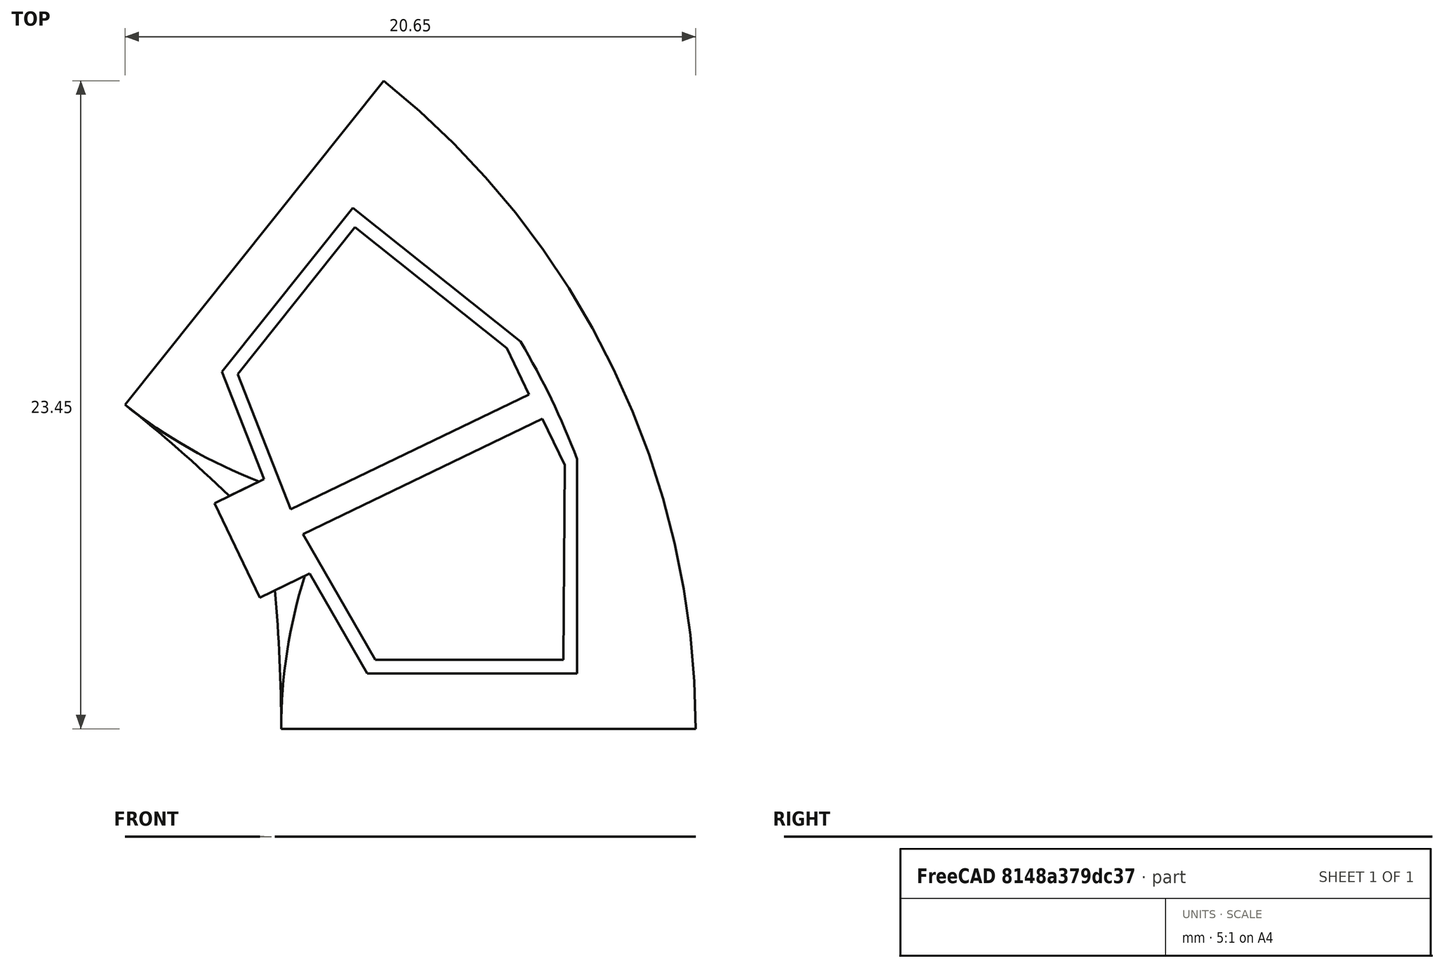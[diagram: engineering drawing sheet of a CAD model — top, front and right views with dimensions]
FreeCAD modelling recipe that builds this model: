
FCSTD DOCUMENT  (FreeCAD 0.18R4 (GitTag))
Label: StatorIRNeedleWinding
License: All rights reserved
LicenseURL: http://en.wikipedia.org/wiki/All_rights_reserved
objects: Sketcher::SketchObject×8, Surface::Filling×5, PartDesign::Body×2, Spreadsheet::Sheet×1
note: 15 computed .brp shape members not serialized (recipe doc carries the construction recipe); baked Part::Feature solids carry a one-line shape summary decoded from their .brp

FEATURE [Spreadsheet::Sheet] Spreadsheet  label="Variables"
  cells = A2=slotNumber; B2(slotNumber)=7; A3=outerDiameter; B3(outerDiameter)=60; A4=innerDiameter; B4(innerDiameter)=30; A5=stackLength; B5(stackLength)=20; A6=stackingFactor; B6(stackingFactor)=0.95; A7=cuttingThickness; B7(cuttingThickness)=0.1; A8=skewAngle; B8(skewAngle)=0; A9=segmentAngle; B9(segmentAngle)==360 / slotNumber; A10=tipHeightReduction; B10(tipHeightReduction)=90; A11=toothThickness; B11(toothThickness)=4; A12=yokeThickness; B12(yokeThickness)=2.5; A13=tipHeight; B13(tipHeight)=2; A14=tipAngle; B14(tipAngle)=120; A15=openingLeft; B15(openingLeft)=1.9; A16=openingRight; B16(openingRight)=1.9; A17=slotIsolation; B17(slotIsolation)=0.5; A18=windingAngle; B18(windingAngle)=35; A19=heightRatio; B19(heightRatio)=45; A20=roundingRadii; B20(roundingRadii)=0.2; A21=backWidth; B21(backWidth)=4.72; A22=backAngle; B22(backAngle)=90; A23=phaseSeparation; B23(phaseSeparation)=1
FEATURE [Sketcher::SketchObject] Sketch003  label="StatorSketch1"
  MapMode = 5
  Support = -> [XY_Plane]
  expr: Constraints[76] = Variables.backWidth
  expr: Constraints[37] = Variables.tipAngle
  expr: Constraints[60] = Variables.backAngle
  expr: Constraints[30] = Variables.tipHeight
  expr: Constraints[28] = Variables.openingRight
  expr: Constraints[32] = Variables.tipHeight * (1 - Variables.tipHeightReduction / 100)
  expr: Constraints[22] = Variables.openingLeft
  expr: Constraints[6] = Variables.outerDiameter / 2
  expr: Constraints[59] = Variables.tipHeight
  expr: Constraints[5] = Variables.segmentAngle
  expr: Constraints[11] = Variables.innerDiameter / 2
  expr: Constraints[54] = Variables.outerDiameter / 2 - Variables.yokeThickness
  expr: Constraints[49] = Variables.tipHeight * (1 - Variables.tipHeightReduction / 100)
  expr: Constraints[58] = Variables.toothThickness / 2
  expr: Constraints[18] = Variables.segmentAngle / 2
  expr: Constraints[50] = Variables.tipAngle
  expr: Constraints[52] = Variables.backAngle
  expr: Constraints[42] = Variables.toothThickness / 2
  sketch-geometry (27):
    g0: LineSegment [constr] StartX=0 StartY=0 StartZ=0 EndX=18.7047 EndY=23.4549 EndZ=0
    g1: LineSegment [constr] StartX=0 StartY=0 StartZ=0 EndX=30 EndY=0 EndZ=0
    g2: ArcOfCircle CenterX=0 CenterY=0 CenterZ=0 NormalX=0 NormalY=0 NormalZ=1 AngleXU=0 Radius=30 StartAngle=0 EndAngle=0.897598
    g3: ArcOfCircle [constr] CenterX=0 CenterY=0 CenterZ=0 NormalX=0 NormalY=0 NormalZ=1 AngleXU=0 Radius=15 StartAngle=0 EndAngle=0.897598
    g4: LineSegment [constr] StartX=12.5834 StartY=8.16445 StartZ=0 EndX=26.1523 EndY=14.6989 EndZ=0
    g5: LineSegment [constr] StartX=14.2288 StartY=4.74764 StartZ=0 EndX=27.7977 EndY=11.2821 EndZ=0
    g6: LineSegment [constr] StartX=27.0291 StartY=13.0165 StartZ=0 EndX=13.5145 EndY=6.50826 EndZ=0
    g7: LineSegment [constr] StartX=0 StartY=0 StartZ=0 EndX=13.5145 EndY=6.50826 EndZ=0
    g8: LineSegment [constr] StartX=12.5834 StartY=8.16445 StartZ=0 EndX=13.5145 EndY=6.50826 EndZ=0
    g9: LineSegment [constr] StartX=13.5145 StartY=6.50826 StartZ=0 EndX=14.2288 EndY=4.74764 EndZ=0
    g10: LineSegment [constr] StartX=13.124 StartY=8.42478 StartZ=0 EndX=14.3853 EndY=9.03222 EndZ=0
    g11: LineSegment StartX=13.124 StartY=8.42478 StartZ=0 EndX=14.3853 EndY=9.03222 EndZ=0
    g12: LineSegment StartX=14.3853 StartY=9.03222 StartZ=0 EndX=12.8601 EndY=12.9183 EndZ=0
    g13: LineSegment StartX=12.8601 StartY=12.9183 StartZ=0 EndX=17.5931 EndY=18.8533 EndZ=0
    g14: LineSegment [constr] StartX=12.8601 StartY=12.9183 StartZ=0 EndX=11.2965 EndY=14.1653 EndZ=0
    g15: LineSegment StartX=17.5931 StartY=18.8533 StartZ=0 EndX=23.6613 EndY=14.0141 EndZ=0
    g16: LineSegment StartX=25.7092 StartY=9.7615 StartZ=0 EndX=25.7092 EndY=2 EndZ=0
    g17: LineSegment StartX=25.7092 StartY=2 StartZ=0 EndX=18.1181 EndY=2 EndZ=0
    g18: LineSegment StartX=18.1181 StartY=2 StartZ=0 EndX=16.0308 EndY=5.61541 EndZ=0
    g19: LineSegment StartX=16.0308 StartY=5.61541 StartZ=0 EndX=14.7694 EndY=5.00797 EndZ=0
    g20: LineSegment [constr] StartX=25.7092 StartY=2 StartZ=0 EndX=25.7092 EndY=0 EndZ=0
    g21: LineSegment StartX=9.35235 StartY=11.7275 StartZ=0 EndX=18.7047 EndY=23.4549 EndZ=0
    g22: LineSegment StartX=30 StartY=0 StartZ=0 EndX=15 EndY=0 EndZ=0
    g23: ArcOfCircle CenterX=-39.4998 CenterY=0 CenterZ=0 NormalX=0 NormalY=0 NormalZ=1 AngleXU=0 Radius=54.4998 StartAngle=0 EndAngle=0.0920195
    g24: ArcOfCircle CenterX=-24.6277 CenterY=-30.8822 CenterZ=0 NormalX=0 NormalY=0 NormalZ=1 AngleXU=0 Radius=54.4998 StartAngle=0.805578 EndAngle=0.897598
    g25: ArcOfCircle CenterX=0 CenterY=0 CenterZ=0 NormalX=0 NormalY=0 NormalZ=1 AngleXU=0 Radius=27.5 StartAngle=0.362875 EndAngle=0.534723
    g26: LineSegment [constr] StartX=23.6613 StartY=14.0141 StartZ=0 EndX=25.7092 EndY=9.7615 EndZ=0
  constraints (77):
    c: Angle(g-1,g1) = 0
    c: Coincident(g0,g-1)
    c: Coincident(g1,g-1)
    c: Coincident(g2,g-1)
    c: Coincident(g2,g0)
    c: Angle(g1,g0) = 0.897598
    c: Radius(g2) = 30
    c: Coincident(g2,g1)
    c: Coincident(g3,g-1)
    c: PointOnObject(g3,g1)
    c: PointOnObject(g3,g0)
    c: Radius(g3) = 15
    c: PointOnObject(g4,g3)
    c: PointOnObject(g4,g2)
    c: PointOnObject(g5,g3)
    c: PointOnObject(g5,g2)
    c: PointOnObject(g6,g2)
    c: PointOnObject(g6,g3)
    c: Angle(g1,g6) = 0.448799
    c: Coincident(g7,g-1)
    c: Coincident(g7,g6)
    c: Coincident(g8,g4)
    c: Distance(g8) = 1.9
    c: Coincident(g8,g6)
    c: Parallel(g4,g6)
    c: Parallel(g5,g6)
    c: Coincident(g9,g6)
    c: Coincident(g9,g5)
    c: Distance(g9) = 1.9
    c: PointOnObject(g10,g4)
    c: Distance(g4,g10) = 2
    c: Angle(g4,g10) = 3.14159
    c: Distance(g10,g10) = 0.2
    c: Coincident(g11,g10)
    c: Coincident(g12,g11)
    c: Coincident(g13,g12)
    c: Coincident(g11,g10)
    c: Angle(g12,g13) = 2.0944
    c: Parallel(g0,g13)
    c: Coincident(g14,g12)
    c: PointOnObject(g14,g0)
    c: Angle(g13,g14) = 1.5708
    c: Distance(g14) = 2
    c: Coincident(g15,g13)
    c: Coincident(g17,g16)
    c: Coincident(g18,g17)
    c: PointOnObject(g18,g5)
    c: Coincident(g19,g18)
    c: PointOnObject(g19,g5)
    c: Distance(g19) = 0.2
    c: Angle(g17,g18) = 2.0944
    c: Parallel(g17,g1)
    c: Angle(g16,g17) = 1.5708
    c: Symmetric(g15,g16,g6)
    c: Distance(g-1,g15) = 27.5
    c: Coincident(g20,g16)
    c: PointOnObject(g20,g1)
    c: Vertical(g20)
    c: DistanceY(g20,g20) = 2
    c: Distance(g5,g18) = 2
    c: Angle(g13,g15) = 1.5708
    c: Coincident(g21,g3)
    c: Coincident(g21,g0)
    c: Coincident(g22,g2)
    c: Coincident(g22,g3)
    c: PointOnObject(g23,g-1)
    c: Coincident(g23,g19)
    c: Coincident(g23,g22)
    c: PointOnObject(g24,g0)
    c: Coincident(g24,g11)
    c: Coincident(g24,g21)
    c: Coincident(g25,g2)
    c: Coincident(g25,g15)
    c: Coincident(g25,g16)
    c: Coincident(g26,g15)
    c: Coincident(g26,g16)
    c: Distance(g26) = 4.72
FEATURE [Sketcher::SketchObject] Sketch  label="StatorStack"
  MapMode = 5
  Support = -> [XY_Plane001]
  expr: Constraints[20] = Variables.innerDiameter / 2
  expr: Constraints[10] = Variables.outerDiameter / 2
  expr: Constraints[9] = Variables.innerDiameter / 2
  expr: Constraints[8] = Variables.stackLength
  sketch-geometry (8):
    g0: LineSegment StartX=-10 StartY=15 StartZ=0 EndX=10 EndY=15 EndZ=0
    g1: LineSegment StartX=10 StartY=15 StartZ=0 EndX=10 EndY=30 EndZ=0
    g2: LineSegment StartX=10 StartY=30 StartZ=0 EndX=-10 EndY=30 EndZ=0
    g3: LineSegment StartX=-10 StartY=30 StartZ=0 EndX=-10 EndY=15 EndZ=0
    g4: LineSegment StartX=-10 StartY=-15 StartZ=0 EndX=10 EndY=-15 EndZ=0
    g5: LineSegment StartX=10 StartY=-15 StartZ=0 EndX=10 EndY=-30 EndZ=0
    g6: LineSegment StartX=10 StartY=-30 StartZ=0 EndX=-10 EndY=-30 EndZ=0
    g7: LineSegment StartX=-10 StartY=-30 StartZ=0 EndX=-10 EndY=-15 EndZ=0
  constraints (22):
    c: Coincident(g0,g1)
    c: Coincident(g1,g2)
    c: Coincident(g2,g3)
    c: Coincident(g3,g0)
    c: Horizontal(g2)
    c: Vertical(g1)
    c: Vertical(g3)
    c: Symmetric(g0,g0,g-2)
    c: DistanceX(g0,g0) = 20
    c: DistanceY(g-1,g0) = 15
    c: DistanceY(g-1,g1) = 30
    c: Coincident(g4,g5)
    c: Coincident(g5,g6)
    c: Coincident(g6,g7)
    c: Coincident(g7,g4)
    c: Horizontal(g6)
    c: Vertical(g5)
    c: Vertical(g7)
    c: Equal(g4,g0)
    c: Symmetric(g4,g4,g-2)
    c: DistanceY(g4,g-1) = 15
    c: Equal(g7,g3)
FEATURE [PartDesign::Body] Body001  label="SideView"
  Group = -> [Sketch]
  Origin = -> Origin001
FEATURE [Sketcher::SketchObject] Sketch005  label="StatorSketch2"
  MapMode = 5
  Support = -> [XY_Plane]
  expr: Constraints[76] = Variables.backWidth
  expr: Constraints[30] = Variables.tipHeight
  expr: Constraints[51] = Variables.tipAngle
  expr: Constraints[28] = Variables.openingRight
  expr: Constraints[37] = Variables.tipAngle
  expr: Constraints[60] = Variables.tipHeight
  expr: Constraints[32] = Variables.tipHeight * (1 - Variables.tipHeightReduction / 100)
  expr: Constraints[61] = Variables.backAngle
  expr: Constraints[6] = Variables.outerDiameter / 2
  expr: Constraints[5] = Variables.segmentAngle
  expr: Constraints[22] = Variables.openingLeft
  expr: Constraints[55] = Variables.outerDiameter / 2 - Variables.yokeThickness
  expr: Constraints[59] = Variables.toothThickness / 2
  expr: Constraints[50] = Variables.tipHeight * (1 - Variables.tipHeightReduction / 100)
  expr: Constraints[18] = Variables.segmentAngle / 2
  expr: Constraints[11] = Variables.innerDiameter / 2
  expr: Constraints[53] = Variables.backAngle
  expr: Constraints[42] = Variables.toothThickness / 2
  sketch-geometry (27):
    g0: LineSegment [constr] StartX=0 StartY=0 StartZ=0 EndX=18.7047 EndY=23.4549 EndZ=0
    g1: LineSegment [constr] StartX=0 StartY=0 StartZ=0 EndX=30 EndY=0 EndZ=0
    g2: ArcOfCircle CenterX=0 CenterY=0 CenterZ=0 NormalX=0 NormalY=0 NormalZ=1 AngleXU=0 Radius=30 StartAngle=0 EndAngle=0.897598
    g3: ArcOfCircle [constr] CenterX=0 CenterY=0 CenterZ=0 NormalX=0 NormalY=0 NormalZ=1 AngleXU=0 Radius=15 StartAngle=0 EndAngle=0.897598
    g4: LineSegment [constr] StartX=12.5834 StartY=8.16445 StartZ=0 EndX=26.1523 EndY=14.6989 EndZ=0
    g5: LineSegment [constr] StartX=14.2288 StartY=4.74764 StartZ=0 EndX=27.7977 EndY=11.2821 EndZ=0
    g6: LineSegment [constr] StartX=27.0291 StartY=13.0165 StartZ=0 EndX=13.5145 EndY=6.50826 EndZ=0
    g7: LineSegment [constr] StartX=0 StartY=0 StartZ=0 EndX=13.5145 EndY=6.50826 EndZ=0
    g8: LineSegment [constr] StartX=12.5834 StartY=8.16445 StartZ=0 EndX=13.5145 EndY=6.50826 EndZ=0
    g9: LineSegment [constr] StartX=13.5145 StartY=6.50826 StartZ=0 EndX=14.2288 EndY=4.74764 EndZ=0
    g10: LineSegment [constr] StartX=14.2051 StartY=8.94544 StartZ=0 EndX=14.3853 EndY=9.03222 EndZ=0
    g11: LineSegment StartX=14.2051 StartY=8.94544 StartZ=0 EndX=14.3853 EndY=9.03222 EndZ=0
    g12: LineSegment StartX=14.3853 StartY=9.03222 StartZ=0 EndX=12.8601 EndY=12.9183 EndZ=0
    g13: LineSegment StartX=12.8601 StartY=12.9183 StartZ=0 EndX=17.5931 EndY=18.8533 EndZ=0
    g14: LineSegment [constr] StartX=12.8601 StartY=12.9183 StartZ=0 EndX=11.2965 EndY=14.1653 EndZ=0
    g15: LineSegment StartX=17.5931 StartY=18.8533 StartZ=0 EndX=23.6613 EndY=14.0141 EndZ=0
    g16: LineSegment [constr] StartX=23.6613 StartY=14.0141 StartZ=0 EndX=25.7092 EndY=9.7615 EndZ=0
    g17: LineSegment StartX=25.7092 StartY=9.7615 StartZ=0 EndX=25.7092 EndY=2 EndZ=0
    g18: LineSegment StartX=25.7092 StartY=2 StartZ=0 EndX=18.1181 EndY=2 EndZ=0
    g19: LineSegment StartX=18.1181 StartY=2 StartZ=0 EndX=16.0308 EndY=5.61541 EndZ=0
    g20: LineSegment StartX=16.0308 StartY=5.61541 StartZ=0 EndX=15.8506 EndY=5.52863 EndZ=0
    g21: LineSegment [constr] StartX=25.7092 StartY=2 StartZ=0 EndX=25.7092 EndY=0 EndZ=0
    g22: LineSegment StartX=9.35235 StartY=11.7275 StartZ=0 EndX=18.7047 EndY=23.4549 EndZ=0
    g23: LineSegment StartX=30 StartY=0 StartZ=0 EndX=15 EndY=0 EndZ=0
    g24: ArcOfCircle CenterX=20.8201 CenterY=26.1075 CenterZ=0 NormalX=0 NormalY=0 NormalZ=1 AngleXU=0 Radius=18.3928 StartAngle=4.03919 EndAngle=4.3445
    g25: ArcOfCircle CenterX=33.3928 CenterY=0 CenterZ=0 NormalX=0 NormalY=0 NormalZ=1 AngleXU=0 Radius=18.3928 StartAngle=2.83628 EndAngle=3.14159
    g26: ArcOfCircle CenterX=0 CenterY=0 CenterZ=0 NormalX=0 NormalY=0 NormalZ=1 AngleXU=0 Radius=27.5 StartAngle=0.362875 EndAngle=0.534723
  constraints (77):
    c: Angle(g-1,g1) = 0
    c: Coincident(g0,g-1)
    c: Coincident(g1,g-1)
    c: Coincident(g2,g-1)
    c: Coincident(g2,g0)
    c: Angle(g1,g0) = 0.897598
    c: Radius(g2) = 30
    c: Coincident(g2,g1)
    c: Coincident(g3,g-1)
    c: PointOnObject(g3,g1)
    c: PointOnObject(g3,g0)
    c: Radius(g3) = 15
    c: PointOnObject(g4,g3)
    c: PointOnObject(g4,g2)
    c: PointOnObject(g5,g3)
    c: PointOnObject(g5,g2)
    c: PointOnObject(g6,g2)
    c: PointOnObject(g6,g3)
    c: Angle(g1,g6) = 0.448799
    c: Coincident(g7,g-1)
    c: Coincident(g7,g6)
    c: Coincident(g8,g4)
    c: Distance(g8) = 1.9
    c: Coincident(g8,g6)
    c: Parallel(g4,g6)
    c: Parallel(g5,g6)
    c: Coincident(g9,g6)
    c: Coincident(g9,g5)
    c: Distance(g9) = 1.9
    c: PointOnObject(g10,g4)
    c: Distance(g4,g10) = 2
    c: Angle(g4,g10) = 3.14159
    c: Distance(g10,g10) = 0.2
    c: Coincident(g11,g10)
    c: Coincident(g12,g11)
    c: Coincident(g13,g12)
    c: Coincident(g11,g10)
    c: Angle(g12,g13) = 2.0944
    c: Parallel(g0,g13)
    c: Coincident(g14,g12)
    c: PointOnObject(g14,g0)
    c: Angle(g13,g14) = 1.5708
    c: Distance(g14) = 2
    c: Coincident(g15,g13)
    c: Coincident(g16,g15)
    c: Coincident(g17,g16)
    c: Coincident(g18,g17)
    c: Coincident(g19,g18)
    c: PointOnObject(g19,g5)
    c: Coincident(g20,g19)
    c: Distance(g20) = 0.2
    c: Angle(g18,g19) = 2.0944
    c: Parallel(g18,g1)
    c: Angle(g17,g18) = 1.5708
    c: Symmetric(g15,g16,g6)
    c: Distance(g-1,g15) = 27.5
    c: Coincident(g21,g17)
    c: PointOnObject(g21,g1)
    c: Vertical(g21)
    c: DistanceY(g21,g21) = 2
    c: Distance(g5,g19) = 2
    c: Angle(g13,g15) = 1.5708
    c: Coincident(g22,g3)
    c: Coincident(g22,g0)
    c: Coincident(g23,g2)
    c: Coincident(g23,g3)
    c: PointOnObject(g24,g22)
    c: Coincident(g24,g11)
    c: Coincident(g24,g22)
    c: Angle(g5,g20) = 3.14159
    c: PointOnObject(g25,g-1)
    c: Coincident(g25,g20)
    c: Coincident(g25,g23)
    c: Coincident(g26,g2)
    c: Coincident(g26,g15)
    c: Coincident(g26,g17)
    c: Distance(g16) = 4.72
FEATURE [Sketcher::SketchObject] Sketch006  label="TerminalLeftSketch"
  MapMode = 5
  Support = -> [XY_Plane]
  expr: Constraints[88] = Variables.phaseSeparation / 2
  expr: Constraints[52] = Variables.toothThickness / 2
  expr: Constraints[48] = Variables.outerDiameter / 2 - Variables.yokeThickness
  expr: Constraints[72] = Variables.slotIsolation
  expr: Constraints[5] = Variables.segmentAngle
  expr: Constraints[29] = Variables.openingRight
  expr: Constraints[43] = Variables.tipAngle
  expr: Constraints[18] = Variables.segmentAngle / 2
  expr: Constraints[36] = Variables.toothThickness / 2
  expr: Constraints[47] = Variables.backWidth
  expr: Constraints[31] = Variables.tipAngle
  expr: Constraints[53] = Variables.tipHeight
  expr: Constraints[54] = Variables.backAngle
  expr: Constraints[11] = Variables.innerDiameter / 2
  expr: Constraints[45] = Variables.backAngle
  expr: Constraints[23] = Variables.openingLeft
  expr: Constraints[6] = Variables.outerDiameter / 2
  sketch-geometry (31):
    g0: LineSegment [constr] StartX=0 StartY=0 StartZ=0 EndX=18.7047 EndY=23.4549 EndZ=0
    g1: LineSegment [constr] StartX=0 StartY=0 StartZ=0 EndX=30 EndY=0 EndZ=0
    g2: ArcOfCircle [constr] CenterX=0 CenterY=0 CenterZ=0 NormalX=0 NormalY=0 NormalZ=1 AngleXU=0 Radius=30 StartAngle=0 EndAngle=0.897598
    g3: ArcOfCircle [constr] CenterX=0 CenterY=0 CenterZ=0 NormalX=0 NormalY=0 NormalZ=1 AngleXU=0 Radius=15 StartAngle=0 EndAngle=0.897598
    g4: LineSegment [constr] StartX=12.5834 StartY=8.16445 StartZ=0 EndX=26.1523 EndY=14.6989 EndZ=0
    g5: LineSegment [constr] StartX=14.2288 StartY=4.74764 StartZ=0 EndX=27.7977 EndY=11.2821 EndZ=0
    g6: LineSegment [constr] StartX=27.0291 StartY=13.0165 StartZ=0 EndX=13.5145 EndY=6.50826 EndZ=0
    g7: LineSegment [constr] StartX=0 StartY=0 StartZ=0 EndX=13.5145 EndY=6.50826 EndZ=0
    g8: LineSegment [constr] StartX=12.5834 StartY=8.16445 StartZ=0 EndX=13.5145 EndY=6.50826 EndZ=0
    g9: LineSegment [constr] StartX=13.5145 StartY=6.50826 StartZ=0 EndX=14.2288 EndY=4.74764 EndZ=0
    g10: LineSegment [constr] StartX=14.3853 StartY=9.03222 StartZ=0 EndX=12.8601 EndY=12.9183 EndZ=0
    g11: LineSegment [constr] StartX=12.8601 StartY=12.9183 StartZ=0 EndX=17.5931 EndY=18.8533 EndZ=0
    g12: LineSegment [constr] StartX=12.8601 StartY=12.9183 StartZ=0 EndX=11.2965 EndY=14.1653 EndZ=0
    g13: LineSegment [constr] StartX=17.5931 StartY=18.8533 StartZ=0 EndX=23.6613 EndY=14.0141 EndZ=0
    g14: LineSegment [constr] StartX=23.6613 StartY=14.0141 StartZ=0 EndX=25.7092 EndY=9.7615 EndZ=0
    g15: LineSegment [constr] StartX=25.7092 StartY=9.7615 StartZ=0 EndX=25.7092 EndY=2 EndZ=0
    g16: LineSegment [constr] StartX=25.7092 StartY=2 StartZ=0 EndX=18.1181 EndY=2 EndZ=0
    g17: LineSegment [constr] StartX=18.1181 StartY=2 StartZ=0 EndX=16.0308 EndY=5.61541 EndZ=0
    g18: LineSegment [constr] StartX=25.7092 StartY=2 StartZ=0 EndX=25.7092 EndY=0 EndZ=0
    g19: LineSegment [constr] StartX=9.35235 StartY=11.7275 StartZ=0 EndX=18.7047 EndY=23.4549 EndZ=0
    g20: LineSegment [constr] StartX=30 StartY=0 StartZ=0 EndX=15 EndY=0 EndZ=0
    g21: LineSegment StartX=23.1613 StartY=13.7733 StartZ=0 EndX=17.6723 EndY=18.1506 EndZ=0
    g22: LineSegment StartX=17.6723 StartY=18.1506 StartZ=0 EndX=13.431 EndY=12.8323 EndZ=0
    g23: LineSegment StartX=13.431 StartY=12.8323 StartZ=0 EndX=15.3486 EndY=7.94645 EndZ=0
    g24: LineSegment StartX=15.3486 StartY=7.94645 StartZ=0 EndX=23.9683 EndY=12.0975 EndZ=0
    g25: LineSegment StartX=23.9683 StartY=12.0975 StartZ=0 EndX=23.1613 EndY=13.7733 EndZ=0
    g26: LineSegment [constr] StartX=17.6723 StartY=18.1506 StartZ=0 EndX=17.984 EndY=18.5415 EndZ=0
    g27: LineSegment [constr] StartX=17.6723 StartY=18.1506 StartZ=0 EndX=17.2813 EndY=18.4624 EndZ=0
    g28: LineSegment [constr] StartX=23.6613 StartY=14.0141 StartZ=0 EndX=23.1613 EndY=13.7733 EndZ=0
    g29: LineSegment [constr] StartX=13.431 StartY=12.8323 StartZ=0 EndX=12.9656 EndY=12.6496 EndZ=0
    g30: LineSegment [constr] StartX=15.3486 StartY=7.94645 StartZ=0 EndX=15.5655 EndY=7.49597 EndZ=0
  constraints (89):
    c: Angle(g-1,g1) = 0
    c: Coincident(g0,g-1)
    c: Coincident(g1,g-1)
    c: Coincident(g2,g-1)
    c: Coincident(g2,g0)
    c: Angle(g1,g0) = 0.897598
    c: Radius(g2) = 30
    c: Coincident(g2,g1)
    c: Coincident(g3,g-1)
    c: PointOnObject(g3,g1)
    c: PointOnObject(g3,g0)
    c: Radius(g3) = 15
    c: PointOnObject(g4,g3)
    c: PointOnObject(g4,g2)
    c: PointOnObject(g5,g3)
    c: PointOnObject(g5,g2)
    c: PointOnObject(g6,g2)
    c: PointOnObject(g6,g3)
    c: Angle(g1,g6) = 0.448799
    c: Coincident(g7,g-1)
    c: Coincident(g7,g6)
    c: Parallel(g7,g6)
    c: Coincident(g8,g4)
    c: Distance(g8) = 1.9
    c: Coincident(g8,g6)
    c: Parallel(g4,g6)
    c: Parallel(g5,g6)
    c: Coincident(g9,g6)
    c: Coincident(g9,g5)
    c: Distance(g9) = 1.9
    c: Coincident(g11,g10)
    c: Angle(g10,g11) = 2.0944
    c: Parallel(g0,g11)
    c: Coincident(g12,g10)
    c: PointOnObject(g12,g0)
    c: Angle(g11,g12) = 1.5708
    c: Distance(g12) = 2
    c: Coincident(g13,g11)
    c: Coincident(g14,g13)
    c: Coincident(g15,g14)
    c: Coincident(g16,g15)
    c: Coincident(g17,g16)
    c: PointOnObject(g17,g5)
    c: Angle(g16,g17) = 2.0944
    c: Parallel(g16,g1)
    c: Angle(g15,g16) = 1.5708
    c: Symmetric(g13,g14,g6)
    c: Distance(g14) = 4.72
    c: Distance(g-1,g13) = 27.5
    c: Coincident(g18,g15)
    c: PointOnObject(g18,g1)
    c: Vertical(g18)
    c: DistanceY(g18,g18) = 2
    c: Distance(g5,g17) = 2
    c: Angle(g11,g13) = 1.5708
    c: Coincident(g19,g3)
    c: Coincident(g19,g0)
    c: Coincident(g20,g2)
    c: Coincident(g20,g3)
    c: Coincident(g22,g21)
    c: Coincident(g23,g22)
    c: Coincident(g24,g23)
    c: Coincident(g25,g24)
    c: Coincident(g25,g21)
    c: Angle(g25,g24) = 1.5708
    c: Coincident(g26,g21)
    c: PointOnObject(g26,g13)
    c: Coincident(g27,g21)
    c: PointOnObject(g27,g11)
    c: Angle(g21,g26) = 1.5708
    c: Angle(g26,g27) = 1.5708
    c: Equal(g27,g26)
    c: Distance(g26) = 0.5
    c: Parallel(g13,g21)
    c: Coincident(g28,g13)
    c: Coincident(g28,g21)
    c: Angle(g25,g28) = 1.5708
    c: Parallel(g11,g22)
    c: Coincident(g29,g22)
    c: PointOnObject(g29,g10)
    c: Angle(g29,g23) = 1.5708
    c: Symmetric(g17,g10,g6)
    c: Parallel(g23,g10)
    c: Equal(g29,g27)
    c: Coincident(g30,g23)
    c: PointOnObject(g30,g6)
    c: Angle(g30,g24) = 1.5708
    c: Parallel(g24,g6)
    c: Distance(g30) = 0.5
FEATURE [Sketcher::SketchObject] Sketch007  label="TerminalRightSketch"
  MapMode = 5
  Support = -> [XY_Plane]
  expr: Constraints[69] = Variables.slotIsolation
  expr: Constraints[45] = Variables.backAngle
  expr: Constraints[52] = Variables.toothThickness / 2
  expr: Constraints[82] = Variables.phaseSeparation / 2
  expr: Constraints[48] = Variables.outerDiameter / 2 - Variables.yokeThickness
  expr: Constraints[53] = Variables.tipHeight
  expr: Constraints[11] = Variables.innerDiameter / 2
  expr: Constraints[54] = Variables.backAngle
  expr: Constraints[6] = Variables.outerDiameter / 2
  expr: Constraints[29] = Variables.openingRight
  expr: Constraints[23] = Variables.openingLeft
  expr: Constraints[31] = Variables.tipAngle
  expr: Constraints[5] = Variables.segmentAngle
  expr: Constraints[43] = Variables.tipAngle
  expr: Constraints[18] = Variables.segmentAngle / 2
  expr: Constraints[36] = Variables.toothThickness / 2
  expr: Constraints[47] = Variables.backWidth
  sketch-geometry (31):
    g0: LineSegment [constr] StartX=0 StartY=0 StartZ=0 EndX=18.7047 EndY=23.4549 EndZ=0
    g1: LineSegment [constr] StartX=0 StartY=0 StartZ=0 EndX=30 EndY=0 EndZ=0
    g2: ArcOfCircle [constr] CenterX=0 CenterY=0 CenterZ=0 NormalX=0 NormalY=0 NormalZ=1 AngleXU=0 Radius=30 StartAngle=0 EndAngle=0.897598
    g3: ArcOfCircle [constr] CenterX=0 CenterY=0 CenterZ=0 NormalX=0 NormalY=0 NormalZ=1 AngleXU=0 Radius=15 StartAngle=0 EndAngle=0.897598
    g4: LineSegment [constr] StartX=12.5834 StartY=8.16445 StartZ=0 EndX=26.1523 EndY=14.6989 EndZ=0
    g5: LineSegment [constr] StartX=14.2288 StartY=4.74764 StartZ=0 EndX=27.7977 EndY=11.2821 EndZ=0
    g6: LineSegment [constr] StartX=27.0291 StartY=13.0165 StartZ=0 EndX=13.5145 EndY=6.50826 EndZ=0
    g7: LineSegment [constr] StartX=0 StartY=0 StartZ=0 EndX=13.5145 EndY=6.50826 EndZ=0
    g8: LineSegment [constr] StartX=12.5834 StartY=8.16445 StartZ=0 EndX=13.5145 EndY=6.50826 EndZ=0
    g9: LineSegment [constr] StartX=13.5145 StartY=6.50826 StartZ=0 EndX=14.2288 EndY=4.74764 EndZ=0
    g10: LineSegment [constr] StartX=14.3853 StartY=9.03222 StartZ=0 EndX=12.8601 EndY=12.9183 EndZ=0
    g11: LineSegment [constr] StartX=12.8601 StartY=12.9183 StartZ=0 EndX=17.5931 EndY=18.8533 EndZ=0
    g12: LineSegment [constr] StartX=12.8601 StartY=12.9183 StartZ=0 EndX=11.2965 EndY=14.1653 EndZ=0
    g13: LineSegment [constr] StartX=17.5931 StartY=18.8533 StartZ=0 EndX=23.6613 EndY=14.0141 EndZ=0
    g14: LineSegment [constr] StartX=23.6613 StartY=14.0141 StartZ=0 EndX=25.7092 EndY=9.7615 EndZ=0
    g15: LineSegment [constr] StartX=25.7092 StartY=9.7615 StartZ=0 EndX=25.7092 EndY=2 EndZ=0
    g16: LineSegment [constr] StartX=25.7092 StartY=2 StartZ=0 EndX=18.1181 EndY=2 EndZ=0
    g17: LineSegment [constr] StartX=18.1181 StartY=2 StartZ=0 EndX=16.0308 EndY=5.61541 EndZ=0
    g18: LineSegment [constr] StartX=25.7092 StartY=2 StartZ=0 EndX=25.7092 EndY=0 EndZ=0
    g19: LineSegment [constr] StartX=9.35235 StartY=11.7275 StartZ=0 EndX=18.7047 EndY=23.4549 EndZ=0
    g20: LineSegment [constr] StartX=30 StartY=0 StartZ=0 EndX=15 EndY=0 EndZ=0
    g21: LineSegment StartX=25.2587 StartY=9.54456 StartZ=0 EndX=25.2092 EndY=2.5 EndZ=0
    g22: LineSegment StartX=25.2092 StartY=2.5 StartZ=0 EndX=18.4068 EndY=2.5 EndZ=0
    g23: LineSegment StartX=18.4068 StartY=2.5 StartZ=0 EndX=15.7825 EndY=7.04548 EndZ=0
    g24: LineSegment StartX=15.7825 StartY=7.04548 StartZ=0 EndX=24.4517 EndY=11.2204 EndZ=0
    g25: LineSegment StartX=24.4517 StartY=11.2204 StartZ=0 EndX=25.2587 EndY=9.54456 EndZ=0
    g26: LineSegment [constr] StartX=25.2587 StartY=9.54456 StartZ=0 EndX=25.7092 EndY=9.7615 EndZ=0
    g27: LineSegment [constr] StartX=25.2092 StartY=2.5 StartZ=0 EndX=25.2092 EndY=2 EndZ=0
    g28: LineSegment [constr] StartX=25.2092 StartY=2.5 StartZ=0 EndX=25.7092 EndY=2.5 EndZ=0
    g29: LineSegment [constr] StartX=24.4517 StartY=11.2204 StartZ=0 EndX=24.2348 EndY=11.6708 EndZ=0
    g30: LineSegment [constr] StartX=18.4068 StartY=2.5 StartZ=0 EndX=17.9738 EndY=2.25 EndZ=0
  constraints (89):
    c: Angle(g-1,g1) = 0
    c: Coincident(g0,g-1)
    c: Coincident(g1,g-1)
    c: Coincident(g2,g-1)
    c: Coincident(g2,g0)
    c: Angle(g1,g0) = 0.897598
    c: Radius(g2) = 30
    c: Coincident(g2,g1)
    c: Coincident(g3,g-1)
    c: PointOnObject(g3,g1)
    c: PointOnObject(g3,g0)
    c: Radius(g3) = 15
    c: PointOnObject(g4,g3)
    c: PointOnObject(g4,g2)
    c: PointOnObject(g5,g3)
    c: PointOnObject(g5,g2)
    c: PointOnObject(g6,g2)
    c: PointOnObject(g6,g3)
    c: Angle(g1,g6) = 0.448799
    c: Coincident(g7,g-1)
    c: Coincident(g7,g6)
    c: Parallel(g7,g6)
    c: Coincident(g8,g4)
    c: Distance(g8) = 1.9
    c: Coincident(g8,g6)
    c: Parallel(g4,g6)
    c: Parallel(g5,g6)
    c: Coincident(g9,g6)
    c: Coincident(g9,g5)
    c: Distance(g9) = 1.9
    c: Coincident(g11,g10)
    c: Angle(g10,g11) = 2.0944
    c: Parallel(g0,g11)
    c: Coincident(g12,g10)
    c: PointOnObject(g12,g0)
    c: Angle(g11,g12) = 1.5708
    c: Distance(g12) = 2
    c: Coincident(g13,g11)
    c: Coincident(g14,g13)
    c: Coincident(g15,g14)
    c: Coincident(g16,g15)
    c: Coincident(g17,g16)
    c: PointOnObject(g17,g5)
    c: Angle(g16,g17) = 2.0944
    c: Parallel(g16,g1)
    c: Angle(g15,g16) = 1.5708
    c: Symmetric(g13,g14,g6)
    c: Distance(g14) = 4.72
    c: Distance(g-1,g13) = 27.5
    c: Coincident(g18,g15)
    c: PointOnObject(g18,g1)
    c: Vertical(g18)
    c: DistanceY(g18,g18) = 2
    c: Distance(g5,g17) = 2
    c: Angle(g11,g13) = 1.5708
    c: Coincident(g19,g3)
    c: Coincident(g19,g0)
    c: Coincident(g20,g2)
    c: Coincident(g20,g3)
    c: Symmetric(g17,g10,g6)
    c: Coincident(g22,g21)
    c: Horizontal(g22)
    c: Coincident(g23,g22)
    c: Coincident(g24,g23)
    c: Coincident(g25,g24)
    c: Coincident(g25,g21)
    c: Coincident(g26,g21)
    c: Coincident(g26,g14)
    c: Angle(g14,g26) = 1.5708
    c: Distance(g26) = 0.5
    c: Coincident(g27,g21)
    c: Vertical(g27)
    c: PointOnObject(g27,g16)
    c: Coincident(g28,g21)
    c: PointOnObject(g28,g15)
    c: Angle(g27,g28) = 1.5708
    c: Equal(g28,g27)
    c: Equal(g27,g26)
    c: Parallel(g24,g6)
    c: Parallel(g25,g14)
    c: PointOnObject(g29,g6)
    c: Angle(g6,g29) = 1.5708
    c: Distance(g29) = 0.5
    c: Coincident(g29,g24)
    c: Parallel(g23,g17)
    c: Coincident(g30,g22)
    c: PointOnObject(g30,g17)
    c: Angle(g23,g30) = 1.5708
    c: Equal(g30,g26)
FEATURE [Sketcher::SketchObject] Sketch008  label="SlotSketch"
  MapMode = 5
  Support = -> [XY_Plane]
  expr: Constraints[50] = Variables.toothThickness / 2
  expr: Constraints[18] = Variables.segmentAngle / 2
  expr: Constraints[30] = Variables.tipAngle
  expr: Constraints[51] = Variables.tipHeight
  expr: Constraints[28] = Variables.openingRight
  expr: Constraints[67] = Variables.backWidth
  expr: Constraints[46] = Variables.outerDiameter / 2 - Variables.yokeThickness
  expr: Constraints[22] = Variables.openingLeft
  expr: Constraints[6] = Variables.outerDiameter / 2
  expr: Constraints[44] = Variables.backAngle
  expr: Constraints[52] = Variables.backAngle
  expr: Constraints[11] = Variables.innerDiameter / 2
  expr: Constraints[5] = Variables.segmentAngle
  expr: Constraints[42] = Variables.tipAngle
  expr: Constraints[35] = Variables.toothThickness / 2
  sketch-geometry (25):
    g0: LineSegment [constr] StartX=0 StartY=0 StartZ=0 EndX=18.7047 EndY=23.4549 EndZ=0
    g1: LineSegment [constr] StartX=0 StartY=0 StartZ=0 EndX=30 EndY=0 EndZ=0
    g2: ArcOfCircle [constr] CenterX=0 CenterY=0 CenterZ=0 NormalX=0 NormalY=0 NormalZ=1 AngleXU=0 Radius=30 StartAngle=0 EndAngle=0.897598
    g3: ArcOfCircle [constr] CenterX=0 CenterY=0 CenterZ=0 NormalX=0 NormalY=0 NormalZ=1 AngleXU=0 Radius=15 StartAngle=0 EndAngle=0.897598
    g4: LineSegment [constr] StartX=12.5834 StartY=8.16445 StartZ=0 EndX=26.1523 EndY=14.6989 EndZ=0
    g5: LineSegment [constr] StartX=14.2288 StartY=4.74764 StartZ=0 EndX=27.7977 EndY=11.2821 EndZ=0
    g6: LineSegment [constr] StartX=27.0291 StartY=13.0165 StartZ=0 EndX=13.5145 EndY=6.50826 EndZ=0
    g7: LineSegment [constr] StartX=0 StartY=0 StartZ=0 EndX=13.5145 EndY=6.50826 EndZ=0
    g8: LineSegment [constr] StartX=12.5834 StartY=8.16445 StartZ=0 EndX=13.5145 EndY=6.50826 EndZ=0
    g9: LineSegment [constr] StartX=13.5145 StartY=6.50826 StartZ=0 EndX=14.2288 EndY=4.74764 EndZ=0
    g10: LineSegment StartX=14.3853 StartY=9.03222 StartZ=0 EndX=12.8601 EndY=12.9183 EndZ=0
    g11: LineSegment StartX=12.8601 StartY=12.9183 StartZ=0 EndX=17.5931 EndY=18.8533 EndZ=0
    g12: LineSegment [constr] StartX=12.8601 StartY=12.9183 StartZ=0 EndX=11.2965 EndY=14.1653 EndZ=0
    g13: LineSegment StartX=17.5931 StartY=18.8533 StartZ=0 EndX=23.6613 EndY=14.0141 EndZ=0
    g14: LineSegment [constr] StartX=23.6613 StartY=14.0141 StartZ=0 EndX=25.7092 EndY=9.7615 EndZ=0
    g15: LineSegment StartX=25.7092 StartY=9.7615 StartZ=0 EndX=25.7092 EndY=2 EndZ=0
    g16: LineSegment StartX=25.7092 StartY=2 StartZ=0 EndX=18.1181 EndY=2 EndZ=0
    g17: LineSegment StartX=18.1181 StartY=2 StartZ=0 EndX=16.0308 EndY=5.61541 EndZ=0
    g18: LineSegment [constr] StartX=25.7092 StartY=2 StartZ=0 EndX=25.7092 EndY=0 EndZ=0
    g19: LineSegment [constr] StartX=9.35235 StartY=11.7275 StartZ=0 EndX=18.7047 EndY=23.4549 EndZ=0
    g20: LineSegment [constr] StartX=30 StartY=0 StartZ=0 EndX=15 EndY=0 EndZ=0
    g21: LineSegment StartX=12.5834 StartY=8.16445 StartZ=0 EndX=14.2288 EndY=4.74764 EndZ=0
    g22: LineSegment StartX=12.5834 StartY=8.16445 StartZ=0 EndX=14.3853 EndY=9.03222 EndZ=0
    g23: LineSegment StartX=14.2288 StartY=4.74764 StartZ=0 EndX=16.0308 EndY=5.61541 EndZ=0
    g24: ArcOfCircle CenterX=0 CenterY=0 CenterZ=0 NormalX=0 NormalY=0 NormalZ=1 AngleXU=0 Radius=27.5 StartAngle=0.362875 EndAngle=0.534723
  constraints (68):
    c: Angle(g-1,g1) = 0
    c: Coincident(g0,g-1)
    c: Coincident(g1,g-1)
    c: Coincident(g2,g-1)
    c: Coincident(g2,g0)
    c: Angle(g1,g0) = 0.897598
    c: Radius(g2) = 30
    c: Coincident(g2,g1)
    c: Coincident(g3,g-1)
    c: PointOnObject(g3,g1)
    c: PointOnObject(g3,g0)
    c: Radius(g3) = 15
    c: PointOnObject(g4,g3)
    c: PointOnObject(g4,g2)
    c: PointOnObject(g5,g3)
    c: PointOnObject(g5,g2)
    c: PointOnObject(g6,g2)
    c: PointOnObject(g6,g3)
    c: Angle(g1,g6) = 0.448799
    c: Coincident(g7,g-1)
    c: Coincident(g7,g6)
    c: Coincident(g8,g4)
    c: Distance(g8) = 1.9
    c: Coincident(g8,g6)
    c: Parallel(g4,g6)
    c: Parallel(g5,g6)
    c: Coincident(g9,g6)
    c: Coincident(g9,g5)
    c: Distance(g9) = 1.9
    c: Coincident(g11,g10)
    c: Angle(g10,g11) = 2.0944
    c: Parallel(g0,g11)
    c: Coincident(g12,g10)
    c: PointOnObject(g12,g0)
    c: Angle(g11,g12) = 1.5708
    c: Distance(g12) = 2
    c: Coincident(g13,g11)
    c: Coincident(g14,g13)
    c: Coincident(g15,g14)
    c: Coincident(g16,g15)
    c: Coincident(g17,g16)
    c: PointOnObject(g17,g5)
    c: Angle(g16,g17) = 2.0944
    c: Parallel(g16,g1)
    c: Angle(g15,g16) = 1.5708
    c: Symmetric(g13,g14,g6)
    c: Distance(g-1,g13) = 27.5
    c: Coincident(g18,g15)
    c: PointOnObject(g18,g1)
    c: Vertical(g18)
    c: DistanceY(g18,g18) = 2
    c: Distance(g5,g17) = 2
    c: Angle(g11,g13) = 1.5708
    c: Coincident(g19,g3)
    c: Coincident(g19,g0)
    c: Coincident(g20,g2)
    c: Coincident(g20,g3)
    c: Symmetric(g17,g10,g6)
    c: Coincident(g21,g4)
    c: Coincident(g21,g5)
    c: Coincident(g22,g21)
    c: Coincident(g22,g10)
    c: Coincident(g23,g21)
    c: Coincident(g23,g17)
    c: Coincident(g24,g-1)
    c: Coincident(g24,g13)
    c: Coincident(g24,g15)
    c: Distance(g14) = 4.72
FEATURE [Surface::Filling] Surface  label="SlotSketch_Surface"
  Anisotropy = false
  BoundaryEdges = -> [Sketch008]
  BoundaryOrder = [0,0,0,0,0,0,0,0,0,0]
  Degree = 3
  Iterations = 2
  MaximumDegree = 8
  MaximumSegments = 9
  PointsOnCurve = 15
  TolAngular = 0.01
  TolCurvature = 0.1
  Tolerance2d = 1e-05
  Tolerance3d = 0.0001
FEATURE [Surface::Filling] Surface001  label="StatorSketch2_Surface"
  Anisotropy = false
  BoundaryEdges = -> [Sketch005]
  BoundaryOrder = [0,0,0,0,0,0,0,0,0,0,0,0,0,0]
  Degree = 3
  Iterations = 2
  MaximumDegree = 8
  MaximumSegments = 9
  PointsOnCurve = 15
  TolAngular = 0.01
  TolCurvature = 0.1
  Tolerance2d = 1e-05
  Tolerance3d = 0.0001
FEATURE [Surface::Filling] Surface002  label="StatorSketch1_Surface"
  Anisotropy = false
  BoundaryEdges = -> [Sketch003]
  BoundaryOrder = [0,0,0,0,0,0,0,0,0,0,0,0,0,0]
  Degree = 3
  Iterations = 2
  MaximumDegree = 8
  MaximumSegments = 9
  PointsOnCurve = 15
  TolAngular = 0.01
  TolCurvature = 0.1
  Tolerance2d = 1e-05
  Tolerance3d = 0.0001
FEATURE [Surface::Filling] Surface003  label="TerminalRightSketch_Surface"
  Anisotropy = false
  BoundaryEdges = -> [Sketch007]
  BoundaryOrder = [0,0,0,0,0]
  Degree = 3
  Iterations = 2
  MaximumDegree = 8
  MaximumSegments = 9
  PointsOnCurve = 15
  TolAngular = 0.01
  TolCurvature = 0.1
  Tolerance2d = 1e-05
  Tolerance3d = 0.0001
FEATURE [Surface::Filling] Surface004  label="TerminalLeftSketch_Surface"
  Anisotropy = false
  BoundaryEdges = -> [Sketch006]
  BoundaryOrder = [0,0,0,0,0]
  Degree = 3
  Iterations = 2
  MaximumDegree = 8
  MaximumSegments = 9
  PointsOnCurve = 15
  TolAngular = 0.01
  TolCurvature = 0.1
  Tolerance2d = 1e-05
  Tolerance3d = 0.0001
FEATURE [Sketcher::SketchObject] Sketch010  label="ToothLine"
  ExternalGeometry = -> [Sketch003]
  MapMode = 5
  Support = -> [XY_Plane]
  expr: Constraints[1] = Variables.toothThickness
  sketch-geometry (1):
    g0: LineSegment StartX=15.2266 StartY=15.8858 StartZ=0 EndX=12.0993 EndY=18.3798 EndZ=0
  constraints (3):
    c: Symmetric(g-3,g-3,g0)
    c: Distance(g0) = 4
    c: Angle(g0,g-3) = 1.5708
FEATURE [Sketcher::SketchObject] Sketch011  label="YokeLine"
  ExternalGeometry = -> [Sketch008]
  MapMode = 5
  Support = -> [XY_Plane]
  expr: Constraints[0] = Variables.yokeThickness
  sketch-geometry (3):
    g0: LineSegment [constr] StartX=23.6613 StartY=14.0141 StartZ=0 EndX=25.7092 EndY=9.7615 EndZ=0
    g1: LineSegment StartX=24.7766 StartY=11.9318 StartZ=0 EndX=27.0291 EndY=13.0165 EndZ=0
    g2: LineSegment [constr] StartX=24.7766 StartY=11.9318 StartZ=0 EndX=24.6852 EndY=11.8878 EndZ=0
  constraints (8):
    c: Distance(g1) = 2.5
    c: Coincident(g0,g-3)
    c: Coincident(g0,g-3)
    c: PointOnObject(g1,g-3)
    c: Coincident(g2,g1)
    c: Angle(g0,g2) = 1.5708
    c: Symmetric(g0,g0,g2)
    c: Parallel(g2,g1)
FEATURE [PartDesign::Body] Body  label="TopView"
  Group = -> [Sketch003,Sketch005,Sketch006,Sketch007,Sketch008,Sketch010,Sketch011]
  Origin = -> Origin
